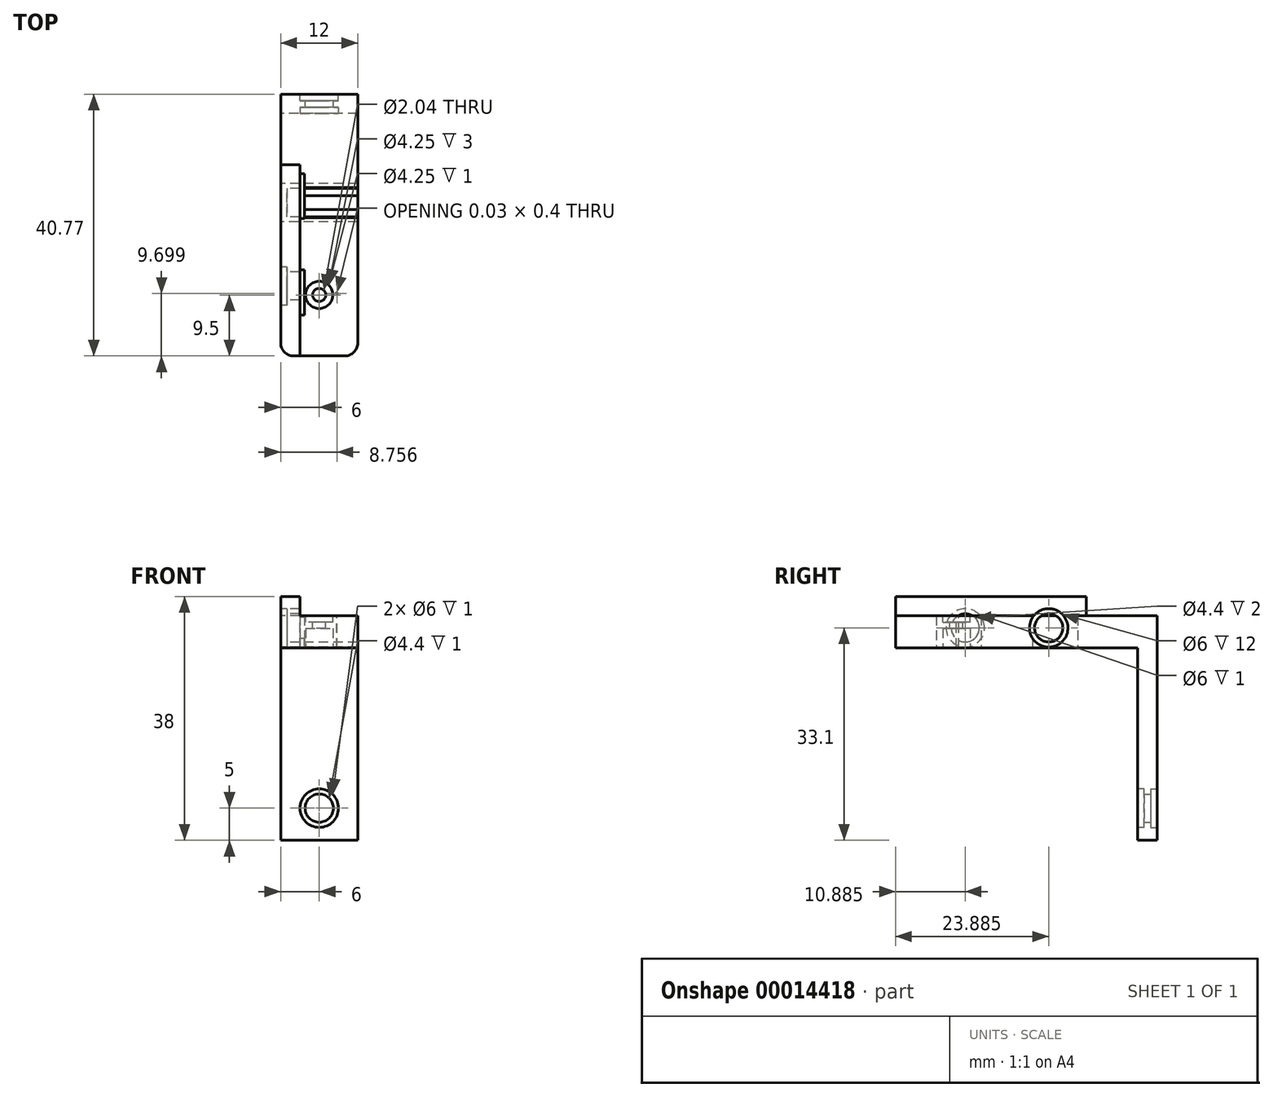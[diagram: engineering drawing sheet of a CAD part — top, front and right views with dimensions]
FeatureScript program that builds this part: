
annotation { "Feature Type Name" : "Feature", "Feature Type Description" : "" }
export const myFeature = defineFeature(function(context is Context, id is Id, definition is map)
    precondition{}
    {
        {
            var Q0;
            Q0=qCreatedBy(makeId("Top.planeOp"),FACE);
            var sketch = newSketch(context, id + "F0", { "sketchPlane" : qUnion([Q0])});
            skArc(sketch, "E0", {"start": v(-2.74, 0.4) * mm, "mid": v(0, -2.77) * mm, "end": v(2.74, 0.4) * mm});
            skPoint(sketch, "E1", {"position": v(0, 12.4) * mm});
            skArc(sketch, "E2", {"start": v(1.88, 12.4) * mm, "mid": v(0, 14.27) * mm, "end": v(-1.88, 12.4) * mm});
            skPoint(sketch, "E3", {"position": v(1.88, 12.4) * mm});
            skPoint(sketch, "E4", {"position": v(2.77, 0) * mm});
            skLineSegment(sketch, "E5", {"start": v(1.87, 12.4) * mm, "end": v(2.77, 0) * mm});
            skLineSegment(sketch, "E6.MirrorCS", {"start": v(-1.87, 12.4) * mm, "end": v(-2.77, 0) * mm});
            skCircle(sketch, "E7", {"center": v(0, 0) * mm, "radius": 2.12 * mm});
            skCircle(sketch, "E8", {"center": v(0, 0) * mm, "radius": 1.02 * mm});
            skCircle(sketch, "E9", {"center": v(0, 0) * mm, "radius": 2.77 * mm});
            skPoint(sketch, "E10", {"position": v(0, -9.5) * mm});
            skLineSegment(sketch, "E11", {"start": v(0, -9.5) * mm, "end": v(6, -9.5) * mm, "construction": true});
            skPoint(sketch, "E12", {"position": v(0, 20.27) * mm});
            skLineSegment(sketch, "E13", {"start": v(0, 20.27) * mm, "end": v(6, 20.27) * mm, "construction": true});
            skLineSegment(sketch, "E14", {"start": v(6, 20.27) * mm, "end": v(6, -9.5) * mm, "construction": true});
            skLineSegment(sketch, "E15.MirrorCS", {"start": v(0, 20.27) * mm, "end": v(-6, 20.27) * mm});
            skLineSegment(sketch, "E16.MirrorCS", {"start": v(-6, 20.27) * mm, "end": v(-6, -7.5) * mm});
            skLineSegment(sketch, "E17.MirrorCS", {"start": v(0, -9.5) * mm, "end": v(-4, -9.5) * mm});
            skPoint(sketch, "E18", {"position": v(0, 23.27) * mm});
            skLineSegment(sketch, "E19", {"start": v(0, 23.27) * mm, "end": v(6, 23.27) * mm});
            skLineSegment(sketch, "E20", {"start": v(6, 20.27) * mm, "end": v(6, 23.27) * mm});
            skLineSegment(sketch, "E21.MirrorCS", {"start": v(0, 23.27) * mm, "end": v(-6, 23.27) * mm});
            skLineSegment(sketch, "E22.MirrorCS", {"start": v(-6, 20.27) * mm, "end": v(-6, 23.27) * mm});
            skLineSegment(sketch, "E23.MirrorCS", {"start": v(6, 20.27) * mm, "end": v(6, -7.5) * mm});
            skLineSegment(sketch, "E24.MirrorCS", {"start": v(0, 20.27) * mm, "end": v(6, 20.27) * mm});
            skLineSegment(sketch, "E25.MirrorCS", {"start": v(0, -9.5) * mm, "end": v(4, -9.5) * mm});
            skPoint(sketch, "E26.visualSharp", {"position": v(-6, -9.5) * mm});
            skArc(sketch, "E26.filletArc", {"start": v(-6, -7.5) * mm, "mid": v(-5.41, -8.91) * mm, "end": v(-4, -9.5) * mm});
            skPoint(sketch, "E27.visualSharp", {"position": v(-6, 23.27) * mm});
            skLineSegment(sketch, "E27.filletArc", {"start": v(-6, 23.27) * mm, "end": v(-6, 23.27) * mm});
            skPoint(sketch, "E28.visualSharp", {"position": v(6, 23.27) * mm});
            skLineSegment(sketch, "E28.filletArc", {"start": v(6, 23.27) * mm, "end": v(6, 23.27) * mm});
            skPoint(sketch, "E29.visualSharp", {"position": v(6, -9.5) * mm});
            skArc(sketch, "E29.filletArc", {"start": v(4, -9.5) * mm, "mid": v(5.41, -8.91) * mm, "end": v(6, -7.5) * mm});
            skPoint(sketch, "E30", {"position": v(-3, 20.27) * mm});
            skLineSegment(sketch, "E31", {"start": v(-3, 20.27) * mm, "end": v(-3, -9.5) * mm});
            skSolve(sketch);
        }
        {
            var Q0;
            {var subQ6=sQuery(id+"F0.wireOp",EDGE,"E2");Q0=makeQuery(id+"F0.imprint","IMPRINT",FACE,{"disambiguationData":[TD([[makeQuery(id+"F0.imprint","IMPRINT",EDGE,{"derivedFrom":subQ6}),-1.0]])]});}
            var Q1;
            Q1=makeQuery(id+"F0.imprint","IMPRINT",FACE,{"disambiguationData":[TD([[makeQuery(id+"F0.imprint","IMPRINT",EDGE,{"derivedFrom":sQuery(id+"F0.wireOp",EDGE,"E15.MirrorCS")}),-1.0]])]});
            var Q2;
            {var subQ5=sQuery(id+"F0.wireOp",EDGE,"E2");Q2=makeQuery(id+"F0.imprint","IMPRINT",FACE,{"disambiguationData":[TD([[makeQuery(id+"F0.imprint","IMPRINT",EDGE,{"derivedFrom":subQ5}),1.0]])]});}
            var Q3;
            Q3=makeQuery(id+"F0.imprint","IMPRINT",FACE,{"disambiguationData":[TD([[makeQuery(id+"F0.imprint","IMPRINT",EDGE,{"derivedFrom":sQuery(id+"F0.wireOp",EDGE,"E7")}),-1.0]])]});
            var Q4;
            Q4=makeQuery(id+"F0.imprint","IMPRINT",FACE,{"disambiguationData":[TD([[makeQuery(id+"F0.imprint","IMPRINT",EDGE,{"derivedFrom":sQuery(id+"F0.wireOp",EDGE,"E7")}),1.0]])]});
            var Q5;
            Q5=makeQuery(id+"F0.imprint","IMPRINT",FACE,{"disambiguationData":[TD([[makeQuery(id+"F0.imprint","IMPRINT",EDGE,{"derivedFrom":sQuery(id+"F0.wireOp",EDGE,"E8")}),1.0]])]});
            var Q6;
            {var subQ3=sQuery(id+"F0.wireOp",EDGE,"E16.MirrorCS");Q6=makeQuery(id+"F0.imprint","IMPRINT",FACE,{"disambiguationData":[TD([[makeQuery(id+"F0.imprint","IMPRINT",EDGE,{"derivedFrom":subQ3}),1.0]])]});}
            extrude(context, id + "F1", {"entities" : qUnion([Q0, Q1, Q2, Q3, Q4, Q5, Q6]), "oppositeDirection" : true, "depth" : 5 * mm});
        }
        {
            var Q0;
            Q0=makeQuery(id+"F0.imprint","IMPRINT",FACE,{"disambiguationData":[TD([[makeQuery(id+"F0.imprint","IMPRINT",EDGE,{"derivedFrom":sQuery(id+"F0.wireOp",EDGE,"E8")}),1.0]])]});
            extrude(context, id + "F2", {"entities" : qUnion([Q0]), "operationType" : NewBodyOperationType.REMOVE, "endBound" : BoundingType.THROUGH_ALL, "oppositeDirection" : true, "depth" : 25 * mm});
        }
        {
            var Q0;
            Q0=makeQuery(id+"F1.opExtrude","CAP_FACE",FACE,{"disambiguationData":[OSD([sQuery(id+"F0.wireOp",EDGE,"E5"),sQuery(id+"F0.wireOp",EDGE,"E6.MirrorCS"),sQuery(id+"F0.wireOp",EDGE,"E9"),sQuery(id+"F0.wireOp",EDGE,"E16.MirrorCS"),sQuery(id+"F0.wireOp",EDGE,"E17.MirrorCS"),sQuery(id+"F0.wireOp",EDGE,"E19"),sQuery(id+"F0.wireOp",EDGE,"E20"),sQuery(id+"F0.wireOp",EDGE,"E21.MirrorCS"),sQuery(id+"F0.wireOp",EDGE,"E22.MirrorCS"),sQuery(id+"F0.wireOp",EDGE,"E23.MirrorCS"),sQuery(id+"F0.wireOp",EDGE,"E25.MirrorCS"),sQuery(id+"F0.wireOp",EDGE,"E26.filletArc"),sQuery(id+"F0.wireOp",EDGE,"E27.filletArc"),sQuery(id+"F0.wireOp",EDGE,"E28.filletArc"),sQuery(id+"F0.wireOp",EDGE,"E29.filletArc")])],"isStart":false});
            var sketch = newSketch(context, id + "F3", { "sketchPlane" : qUnion([Q0])});
            skCircle(sketch, "E32", {"center": v(0, 0) * mm, "radius": 2.12 * mm});
            skCircle(sketch, "E33", {"center": v(0, 0) * mm, "radius": 1.02 * mm});
            skSolve(sketch);
        }
        {
            var Q0;
            Q0=makeQuery(id+"F3.imprint","IMPRINT",FACE,{"disambiguationData":[TD([[makeQuery(id+"F3.imprint","IMPRINT",EDGE,{"derivedFrom":sQuery(id+"F3.wireOp",EDGE,"E32")}),1.0]])]});
            extrude(context, id + "F4", {"entities" : qUnion([Q0]), "operationType" : NewBodyOperationType.REMOVE, "oppositeDirection" : true, "depth" : 3 * mm});
        }
        {
            var Q0;
            {var subQ3=sQuery(id+"F0.wireOp",EDGE,"E16.MirrorCS");Q0=makeQuery(id+"F0.imprint","IMPRINT",FACE,{"disambiguationData":[TD([[makeQuery(id+"F0.imprint","IMPRINT",EDGE,{"derivedFrom":subQ3}),1.0]])]});}
            extrude(context, id + "F5", {"entities" : qUnion([Q0]), "operationType" : NewBodyOperationType.ADD, "depth" : 3 * mm});
        }
        {
            var Q0;
            {var subQ0=sQuery(id+"F0.wireOp",EDGE,"E16.MirrorCS");var subQ1=sQuery(id+"F0.wireOp",EDGE,"E22.MirrorCS");Q0=makeQuery(id+"F5.boolean.opBoolean","MERGE",FACE,{"derivedFrom":[makeQuery(id+"FVNe3gR9TBvJjzu_1.boolean.opBoolean","MERGE",FACE,{"derivedFrom":[makeQuery(id+"F1.opExtrude","SWEPT_FACE",FACE,{"disambiguationData":[OSD([subQ0,subQ1])]}),makeQuery(id+"FVNe3gR9TBvJjzu_1.opExtrude","SWEPT_FACE",FACE,{"disambiguationData":[OSD([subQ1])]})]}),makeQuery(id+"F5.opExtrude","SWEPT_FACE",FACE,{"disambiguationData":[OSD([subQ0])]})]});}
            var sketch = newSketch(context, id + "F6", { "sketchPlane" : qUnion([Q0])});
            skCircle(sketch, "E34.MirrorC", {"center": v(-14.39, -1.9) * mm, "radius": 2.2 * mm});
            skCircle(sketch, "E35.MirrorC", {"center": v(-14.39, -1.9) * mm, "radius": 3 * mm});
            skLineSegment(sketch, "E36", {"start": v(-7.89, -5) * mm, "end": v(-7.89, 3) * mm, "construction": true});
            skCircle(sketch, "E37.MirrorC", {"center": v(-1.39, -1.9) * mm, "radius": 3 * mm});
            skCircle(sketch, "E38.MirrorC", {"center": v(-1.39, -1.9) * mm, "radius": 2.2 * mm});
            skSolve(sketch);
        }
        {
            var Q0;
            Q0=makeQuery(id+"F1.opExtrude","CAP_FACE",FACE,{"disambiguationData":[OSD([sQuery(id+"F0.wireOp",EDGE,"E5"),sQuery(id+"F0.wireOp",EDGE,"E6.MirrorCS"),sQuery(id+"F0.wireOp",EDGE,"E9"),sQuery(id+"F0.wireOp",EDGE,"E16.MirrorCS"),sQuery(id+"F0.wireOp",EDGE,"E17.MirrorCS"),sQuery(id+"F0.wireOp",EDGE,"E19"),sQuery(id+"F0.wireOp",EDGE,"E20"),sQuery(id+"F0.wireOp",EDGE,"E21.MirrorCS"),sQuery(id+"F0.wireOp",EDGE,"E22.MirrorCS"),sQuery(id+"F0.wireOp",EDGE,"E23.MirrorCS"),sQuery(id+"F0.wireOp",EDGE,"E25.MirrorCS"),sQuery(id+"F0.wireOp",EDGE,"E26.filletArc"),sQuery(id+"F0.wireOp",EDGE,"E27.filletArc"),sQuery(id+"F0.wireOp",EDGE,"E28.filletArc"),sQuery(id+"F0.wireOp",EDGE,"E29.filletArc")])],"isStart":false});
            var sketch = newSketch(context, id + "F7", { "sketchPlane" : qUnion([Q0])});
            skLineSegment(sketch, "E39", {"start": v(-6, -7.89) * mm, "end": v(-2.3, -7.89) * mm, "construction": true});
            skPoint(sketch, "E39.endSnap0", {"position": v(-6, -7.89) * mm});
            skPoint(sketch, "E40", {"position": v(-3, -7.89) * mm});
            skLineSegment(sketch, "E41", {"start": v(-3, -7.89) * mm, "end": v(-3, -18.88) * mm, "construction": true});
            skPoint(sketch, "E42", {"position": v(-3, -11.88) * mm});
            skLineSegment(sketch, "E43", {"start": v(-2.3, -7.88) * mm, "end": v(-2.3, -18.88) * mm, "construction": true});
            skLineSegment(sketch, "E44", {"start": v(-3, -18.88) * mm, "end": v(-2.3, -18.88) * mm, "construction": true});
            skLineSegment(sketch, "E45", {"start": v(-3, -11.88) * mm, "end": v(-3, -18.88) * mm});
            skLineSegment(sketch, "E46", {"start": v(-3, -18.88) * mm, "end": v(-2.3, -18.88) * mm});
            skLineSegment(sketch, "E47", {"start": v(-3, -11.88) * mm, "end": v(-2.3, -11.88) * mm});
            skLineSegment(sketch, "E48", {"start": v(-2.3, -11.88) * mm, "end": v(-2.3, -18.88) * mm});
            skLineSegment(sketch, "E49.MirrorCS", {"start": v(-3, -3.89) * mm, "end": v(-2.3, -3.89) * mm});
            skLineSegment(sketch, "E50.MirrorCS", {"start": v(-3, -3.89) * mm, "end": v(-3, 3.11) * mm});
            skLineSegment(sketch, "E51.MirrorCS", {"start": v(-2.3, -3.89) * mm, "end": v(-2.3, 3.11) * mm});
            skLineSegment(sketch, "E52.MirrorCS", {"start": v(-3, 3.11) * mm, "end": v(-2.3, 3.11) * mm});
            skSolve(sketch);
        }
        {
            var Q0;
            {var subQ5=sQuery(id+"F7.wireOp",EDGE,"E52.MirrorCS");Q0=makeQuery(id+"F7.imprint","IMPRINT",FACE,{"disambiguationData":[TD([[makeQuery(id+"F7.imprint","IMPRINT",EDGE,{"derivedFrom":subQ5}),-1.0]])]});}
            var Q1;
            {var subQ0=makeQuery(id+"F4.boolean.opBoolean","COPY",EDGE,{"derivedFrom":makeQuery(id+"F4.opExtrude","CAP_EDGE",EDGE,{"disambiguationData":[OSD([sQuery(id+"F3.wireOp",EDGE,"E32")])],"isStart":true})});var subQ3=sQuery(id+"F7.wireOp",EDGE,"E50.MirrorCS");var subQ4=makeQuery(id+"F7.imprint","INTERSECT",VERTEX,{"disambiguationData":[OD(0.0)],"derivedFrom":[subQ0,subQ3]});Q1=makeQuery(id+"F7.imprint","IMPRINT",FACE,{"disambiguationData":[TD([[makeQuery(id+"F7.imprint","IMPRINT",EDGE,{"disambiguationData":[TD([[subQ4,-1.0]])],"derivedFrom":subQ3}),-1.0]])]});}
            var Q2;
            {var subQ3=sQuery(id+"F7.wireOp",EDGE,"E49.MirrorCS");Q2=makeQuery(id+"F7.imprint","IMPRINT",FACE,{"disambiguationData":[TD([[makeQuery(id+"F7.imprint","IMPRINT",EDGE,{"derivedFrom":subQ3}),1.0]])]});}
            var Q3;
            Q3=makeQuery(id+"F7.imprint","IMPRINT",FACE,{"disambiguationData":[TD([[makeQuery(id+"F7.imprint","IMPRINT",EDGE,{"derivedFrom":sQuery(id+"F7.wireOp",EDGE,"E45")}),1.0]])]});
            extrude(context, id + "F8", {"entities" : qUnion([Q0, Q1, Q2, Q3]), "operationType" : NewBodyOperationType.REMOVE, "oppositeDirection" : true, "depth" : 7 * mm});
        }
        {
            var Q0;
            Q0=makeQuery(id+"F6.imprint","IMPRINT",FACE,{"disambiguationData":[TD([[makeQuery(id+"F6.imprint","IMPRINT",EDGE,{"derivedFrom":sQuery(id+"F6.wireOp",EDGE,"E34.MirrorC")}),-1.0]])]});
            var Q1;
            Q1=makeQuery(id+"F6.imprint","IMPRINT",FACE,{"disambiguationData":[TD([[makeQuery(id+"F6.imprint","IMPRINT",EDGE,{"derivedFrom":sQuery(id+"F6.wireOp",EDGE,"E38.MirrorC")}),1.0]])]});
            extrude(context, id + "F9", {"entities" : qUnion([Q0, Q1]), "operationType" : NewBodyOperationType.REMOVE, "endBound" : BoundingType.UP_TO_NEXT, "oppositeDirection" : true, "depth" : 25 * mm});
        }
        {
            var Q0;
            Q0=makeQuery(id+"F6.imprint","IMPRINT",FACE,{"disambiguationData":[TD([[makeQuery(id+"F6.imprint","IMPRINT",EDGE,{"derivedFrom":sQuery(id+"F6.wireOp",EDGE,"E34.MirrorC")}),1.0]])]});
            var Q1;
            Q1=makeQuery(id+"F6.imprint","IMPRINT",FACE,{"disambiguationData":[TD([[makeQuery(id+"F6.imprint","IMPRINT",EDGE,{"derivedFrom":sQuery(id+"F6.wireOp",EDGE,"E37.MirrorC")}),1.0]])]});
            extrude(context, id + "F10", {"entities" : qUnion([Q0, Q1]), "operationType" : NewBodyOperationType.REMOVE, "oppositeDirection" : true, "depth" : 1 * mm});
        }
        {
            var Q0;
            Q0=makeQuery(id+"F1.opExtrude","SWEPT_FACE",FACE,{"disambiguationData":[OSD([sQuery(id+"F0.wireOp",EDGE,"E19"),sQuery(id+"F0.wireOp",EDGE,"E21.MirrorCS")])]});
            extrude(context, id + "F11", {"entities" : qUnion([Q0]), "operationType" : NewBodyOperationType.ADD, "depth" : 8 * mm});
        }
        {
            var Q0;
            {var subQ0=sQuery(id+"F0.wireOp",EDGE,"E19");var subQ1=sQuery(id+"F0.wireOp",EDGE,"E21.MirrorCS");Q0=makeQuery(id+"F11.boolean.opBoolean","MERGE",FACE,{"derivedFrom":[makeQuery(id+"F1.opExtrude","CAP_FACE",FACE,{"disambiguationData":[OSD([sQuery(id+"F0.wireOp",EDGE,"E5"),sQuery(id+"F0.wireOp",EDGE,"E6.MirrorCS"),sQuery(id+"F0.wireOp",EDGE,"E9"),sQuery(id+"F0.wireOp",EDGE,"E16.MirrorCS"),sQuery(id+"F0.wireOp",EDGE,"E17.MirrorCS"),subQ0,sQuery(id+"F0.wireOp",EDGE,"E20"),subQ1,sQuery(id+"F0.wireOp",EDGE,"E22.MirrorCS"),sQuery(id+"F0.wireOp",EDGE,"E23.MirrorCS"),sQuery(id+"F0.wireOp",EDGE,"E25.MirrorCS"),sQuery(id+"F0.wireOp",EDGE,"E26.filletArc"),sQuery(id+"F0.wireOp",EDGE,"E29.filletArc")])],"isStart":true}),makeQuery(id+"F11.opExtrude","SWEPT_FACE",FACE,{"disambiguationData":[OSD([subQ0,subQ1]),TDD([makeQuery(id+"F1.opExtrude","CAP_EDGE",EDGE,{"disambiguationData":[OSD([subQ0,subQ1])],"isStart":true})])]})]});}
            var sketch = newSketch(context, id + "F12", { "sketchPlane" : qUnion([Q0])});
            skPoint(sketch, "E53", {"position": v(6, 31.27) * mm});
            skPoint(sketch, "E54", {"position": v(6, 28.27) * mm});
            skLineSegment(sketch, "E55", {"start": v(6, 28.27) * mm, "end": v(-6, 28.27) * mm});
            skLineSegment(sketch, "E56", {"start": v(-6, 28.27) * mm, "end": v(-6, 31.27) * mm});
            skLineSegment(sketch, "E57", {"start": v(-6, 31.27) * mm, "end": v(6, 31.27) * mm});
            skLineSegment(sketch, "E58", {"start": v(6, 28.27) * mm, "end": v(6, 31.27) * mm});
            skSolve(sketch);
        }
        {
            var Q0;
            Q0=makeQuery(id+"F12.imprint","IMPRINT",FACE,{"disambiguationData":[TD([[makeQuery(id+"F12.imprint","IMPRINT",EDGE,{"derivedFrom":sQuery(id+"F12.wireOp",EDGE,"E55")}),-1.0]])]});
            extrude(context, id + "F13", {"entities" : qUnion([Q0]), "operationType" : NewBodyOperationType.ADD, "oppositeDirection" : true, "depth" : 35 * mm});
        }
        {
            var Q0;
            Q0=makeQuery(id+"F13.boolean.opBoolean","MERGE",FACE,{"derivedFrom":[makeQuery(id+"F11.opExtrude","CAP_FACE",FACE,{"disambiguationData":[OSD([sQuery(id+"F0.wireOp",EDGE,"E19"),sQuery(id+"F0.wireOp",EDGE,"E21.MirrorCS")])],"isStart":false}),makeQuery(id+"F13.opExtrude","SWEPT_FACE",FACE,{"disambiguationData":[OSD([sQuery(id+"F12.wireOp",EDGE,"E57")])]})]});
            var sketch = newSketch(context, id + "F14", { "sketchPlane" : qUnion([Q0])});
            skPoint(sketch, "E59", {"position": v(6, -30) * mm});
            skPoint(sketch, "E60", {"position": v(6, -35) * mm});
            skLineSegment(sketch, "E61", {"start": v(6, -30) * mm, "end": v(-6, -30) * mm, "construction": true});
            skPoint(sketch, "E62", {"position": v(0, -30) * mm});
            skCircle(sketch, "E63", {"center": v(0, -30) * mm, "radius": 3 * mm});
            skCircle(sketch, "E64", {"center": v(0, -30) * mm, "radius": 2.2 * mm});
            skSolve(sketch);
        }
        {
            var Q0;
            Q0=makeQuery(id+"F14.imprint","IMPRINT",FACE,{"disambiguationData":[TD([[makeQuery(id+"F14.imprint","IMPRINT",EDGE,{"derivedFrom":sQuery(id+"F14.wireOp",EDGE,"E64")}),1.0]])]});
            extrude(context, id + "F15", {"entities" : qUnion([Q0]), "operationType" : NewBodyOperationType.REMOVE, "endBound" : BoundingType.THROUGH_ALL, "oppositeDirection" : true, "depth" : 25 * mm});
        }
        {
            var Q0;
            Q0=makeQuery(id+"F14.imprint","IMPRINT",FACE,{"disambiguationData":[TD([[makeQuery(id+"F14.imprint","IMPRINT",EDGE,{"derivedFrom":sQuery(id+"F14.wireOp",EDGE,"E63")}),1.0]])]});
            extrude(context, id + "F16", {"entities" : qUnion([Q0]), "operationType" : NewBodyOperationType.REMOVE, "oppositeDirection" : true, "depth" : 1 * mm});
        }
        {
            var Q0;
            Q0=makeQuery(id+"F13.opExtrude","SWEPT_FACE",FACE,{"disambiguationData":[OSD([sQuery(id+"F12.wireOp",EDGE,"E55")])]});
            var sketch = newSketch(context, id + "F17", { "sketchPlane" : qUnion([Q0])});
            skCircle(sketch, "E65", {"center": v(0, -30) * mm, "radius": 3 * mm});
            skCircle(sketch, "E66", {"center": v(0, -30) * mm, "radius": 2.2 * mm});
            skSolve(sketch);
        }
        {
            var Q0;
            Q0=makeQuery(id+"F17.imprint","IMPRINT",FACE,{"disambiguationData":[TD([[makeQuery(id+"F17.imprint","IMPRINT",EDGE,{"derivedFrom":sQuery(id+"F17.wireOp",EDGE,"E65")}),1.0]])]});
            extrude(context, id + "F18", {"entities" : qUnion([Q0]), "operationType" : NewBodyOperationType.REMOVE, "oppositeDirection" : true, "depth" : 1 * mm});
        }
        {
            var Q0;
            Q0=makeQuery(id+"F0.imprint","IMPRINT",FACE,{"disambiguationData":[TD([[makeQuery(id+"F0.imprint","IMPRINT",EDGE,{"derivedFrom":sQuery(id+"F0.wireOp",EDGE,"E7")}),1.0]])]});
            extrude(context, id + "F19", {"entities" : qUnion([Q0]), "operationType" : NewBodyOperationType.REMOVE, "oppositeDirection" : true, "depth" : 1 * mm});
        }
    });
